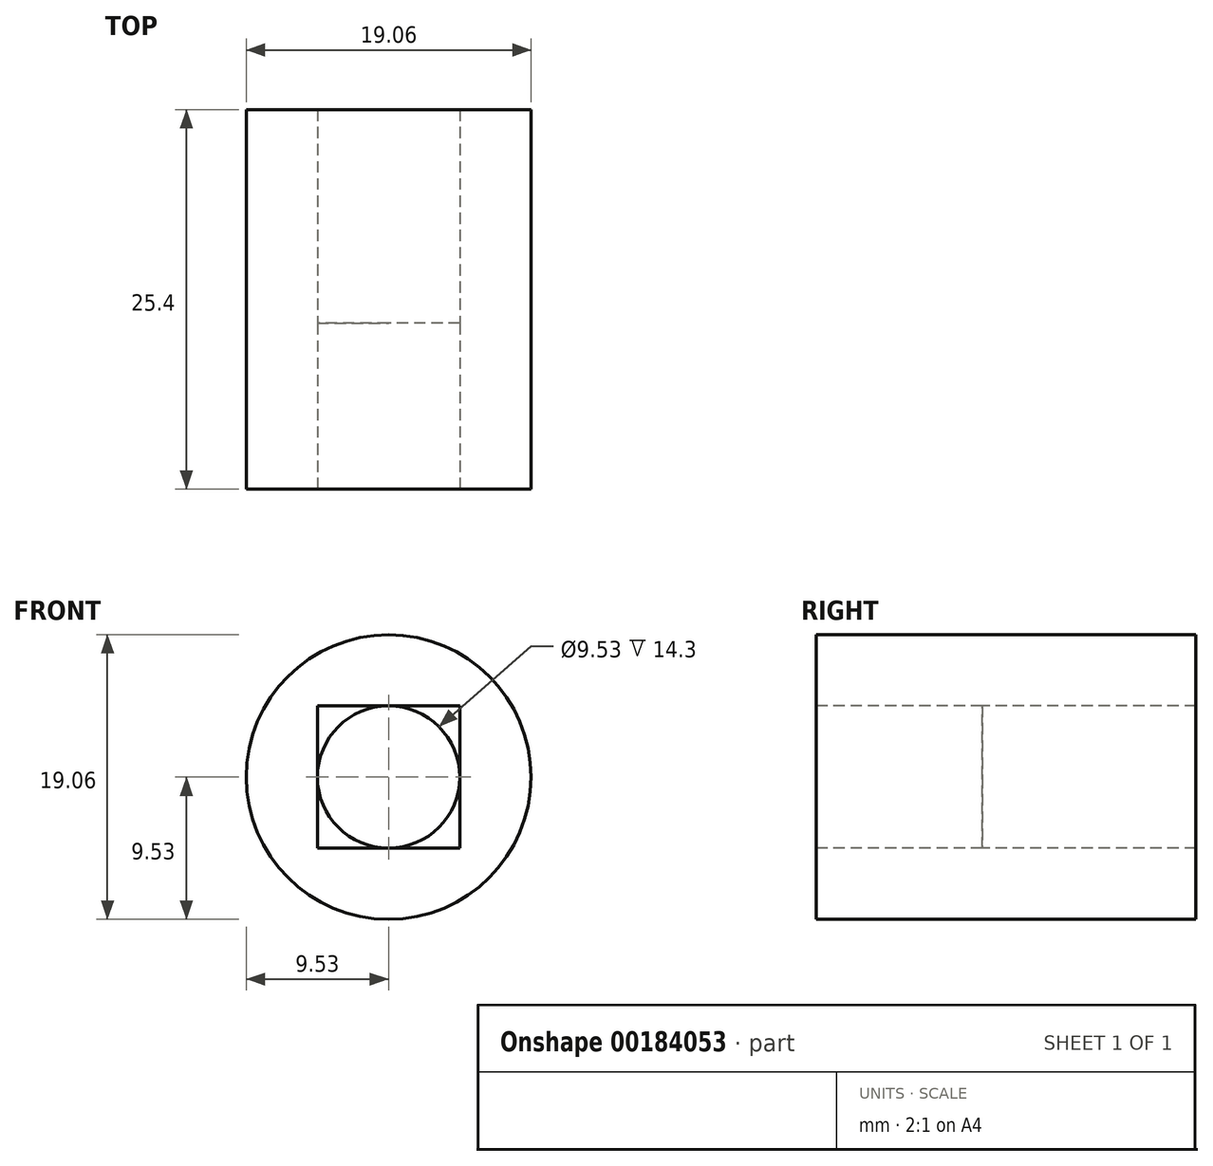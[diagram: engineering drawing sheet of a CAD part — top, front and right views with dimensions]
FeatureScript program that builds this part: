
annotation { "Feature Type Name" : "Feature", "Feature Type Description" : "" }
export const myFeature = defineFeature(function(context is Context, id is Id, definition is map)
    precondition{}
    {
        {
            var Q0;
            Q0=qCreatedBy(makeId("Front.planeOp"),FACE);
            var sketch = newSketch(context, id + "F0", { "sketchPlane" : qUnion([Q0])});
            skCircle(sketch, "E0", {"center": v(0, 0) * mm, "radius": 9.53 * mm});
            skSolve(sketch);
        }
        {
            var Q0;
            Q0 = qSketchRegion(id + "F0", true);
            extrude(context, id + "F1", {"entities" : qUnion([Q0]), "depth" : 25.4 * mm});
        }
        {
            var Q0;
            Q0=makeQuery(id+"F1.opExtrude","CAP_FACE",FACE,{"disambiguationData":[OSD([sQuery(id+"F0.wireOp",EDGE,"E0")])],"isStart":false});
            var sketch = newSketch(context, id + "F2", { "sketchPlane" : qUnion([Q0])});
            skLineSegment(sketch, "E1.bottom", {"start": v(4.76, -4.76) * mm, "end": v(-4.76, -4.76) * mm});
            skLineSegment(sketch, "E1.top", {"start": v(4.76, 4.76) * mm, "end": v(-4.76, 4.76) * mm});
            skLineSegment(sketch, "E1.left", {"start": v(4.76, -4.76) * mm, "end": v(4.76, 4.76) * mm});
            skLineSegment(sketch, "E1.right", {"start": v(-4.76, -4.76) * mm, "end": v(-4.76, 4.76) * mm});
            skPoint(sketch, "E1.middle", {"position": v(0, 0) * mm});
            skPoint(sketch, "E2.middle", {"position": v(4.76, 4.76) * mm});
            skCircle(sketch, "E3", {"center": v(0, 0) * mm, "radius": 4.76 * mm});
            skSolve(sketch);
        }
        {
            var Q0;
            {var subQ0=sQuery(id+"F2.wireOp",EDGE,"E3");var subQ1=makeQuery(id+"F2.imprint","INTERSECT",VERTEX,{"derivedFrom":[sQuery(id+"F2.wireOp",EDGE,"E1.top"),subQ0]});Q0=makeQuery(id+"F2.imprint","IMPRINT",FACE,{"disambiguationData":[TD([[makeQuery(id+"F2.imprint","IMPRINT",EDGE,{"disambiguationData":[TD([[subQ1,1.0]])],"derivedFrom":subQ0}),1.0]])]});}
            extrude(context, id + "F3", {"entities" : qUnion([Q0]), "operationType" : NewBodyOperationType.REMOVE, "endBound" : BoundingType.THROUGH_ALL, "oppositeDirection" : true, "depth" : 25.4 * mm});
        }
        {
            var Q0;
            Q0 = qSketchRegion(id + "F2", true);
            extrude(context, id + "F4", {"entities" : qUnion([Q0]), "operationType" : NewBodyOperationType.REMOVE, "oppositeDirection" : true, "depth" : 11.1 * mm});
        }
    });
